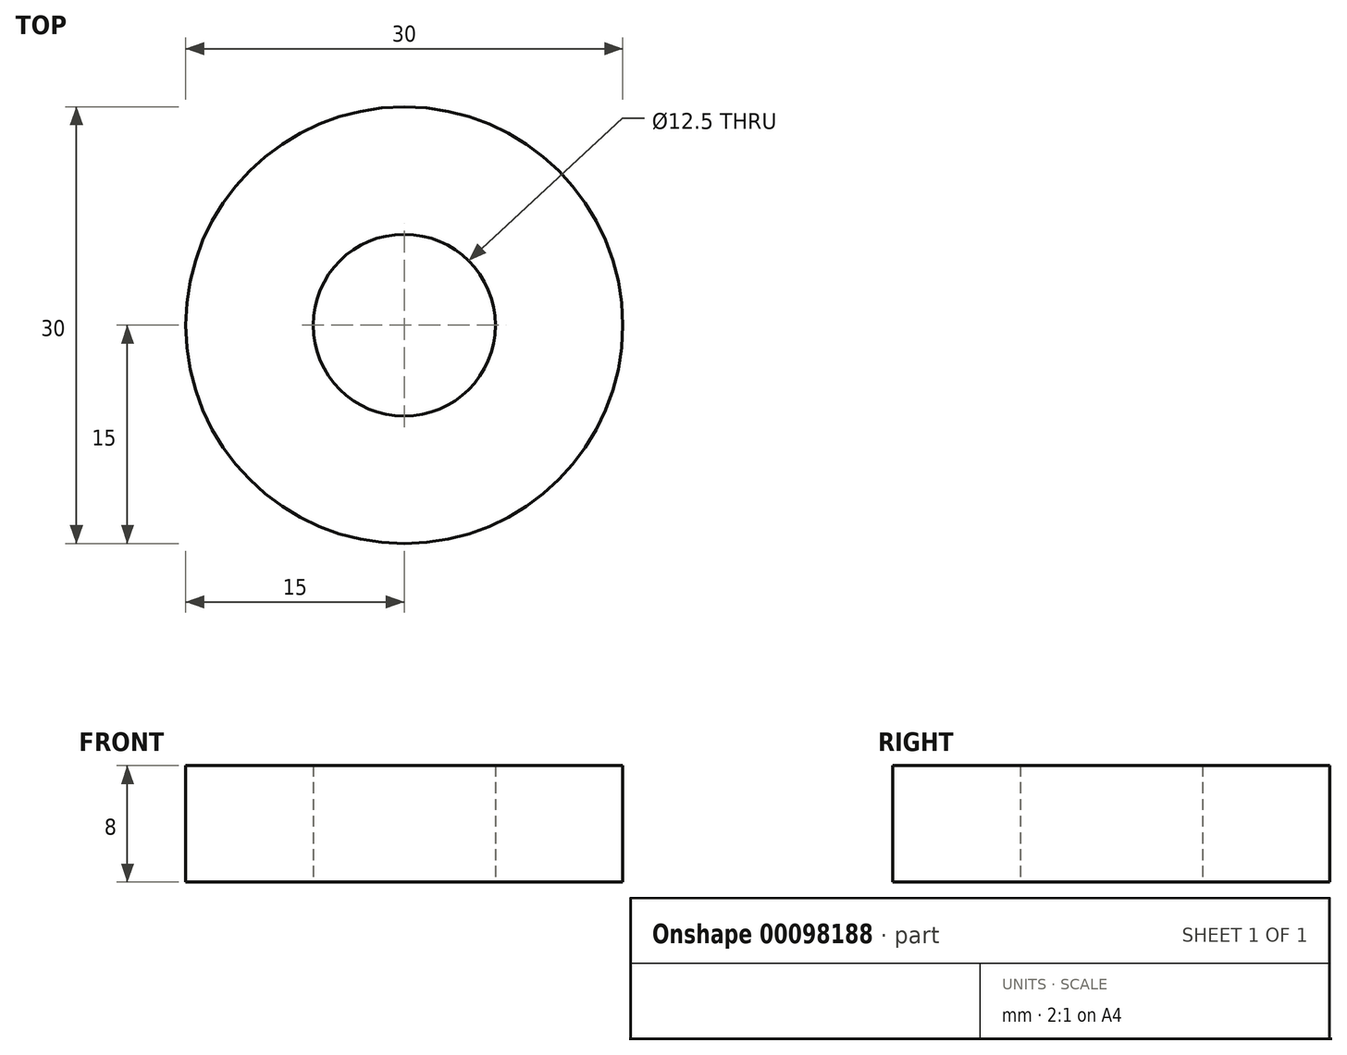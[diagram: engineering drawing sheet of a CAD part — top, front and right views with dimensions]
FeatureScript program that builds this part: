
annotation { "Feature Type Name" : "Feature", "Feature Type Description" : "" }
export const myFeature = defineFeature(function(context is Context, id is Id, definition is map)
    precondition{}
    {
        {
            var Q0;
            Q0=qCreatedBy(makeId("Top.planeOp"),FACE);
            var sketch = newSketch(context, id + "F0", { "sketchPlane" : qUnion([Q0])});
            skCircle(sketch, "E0", {"center": v(0, 0) * mm, "radius": 6.25 * mm});
            skCircle(sketch, "E1", {"center": v(0, 0) * mm, "radius": 15 * mm});
            skSolve(sketch);
        }
        {
            var Q0;
            Q0 = qSketchRegion(id + "F0", true);
            extrude(context, id + "F1", {"entities" : qUnion([Q0]), "depth" : 8 * mm, "offsetDistance" : 25 * mm});
        }
    });
